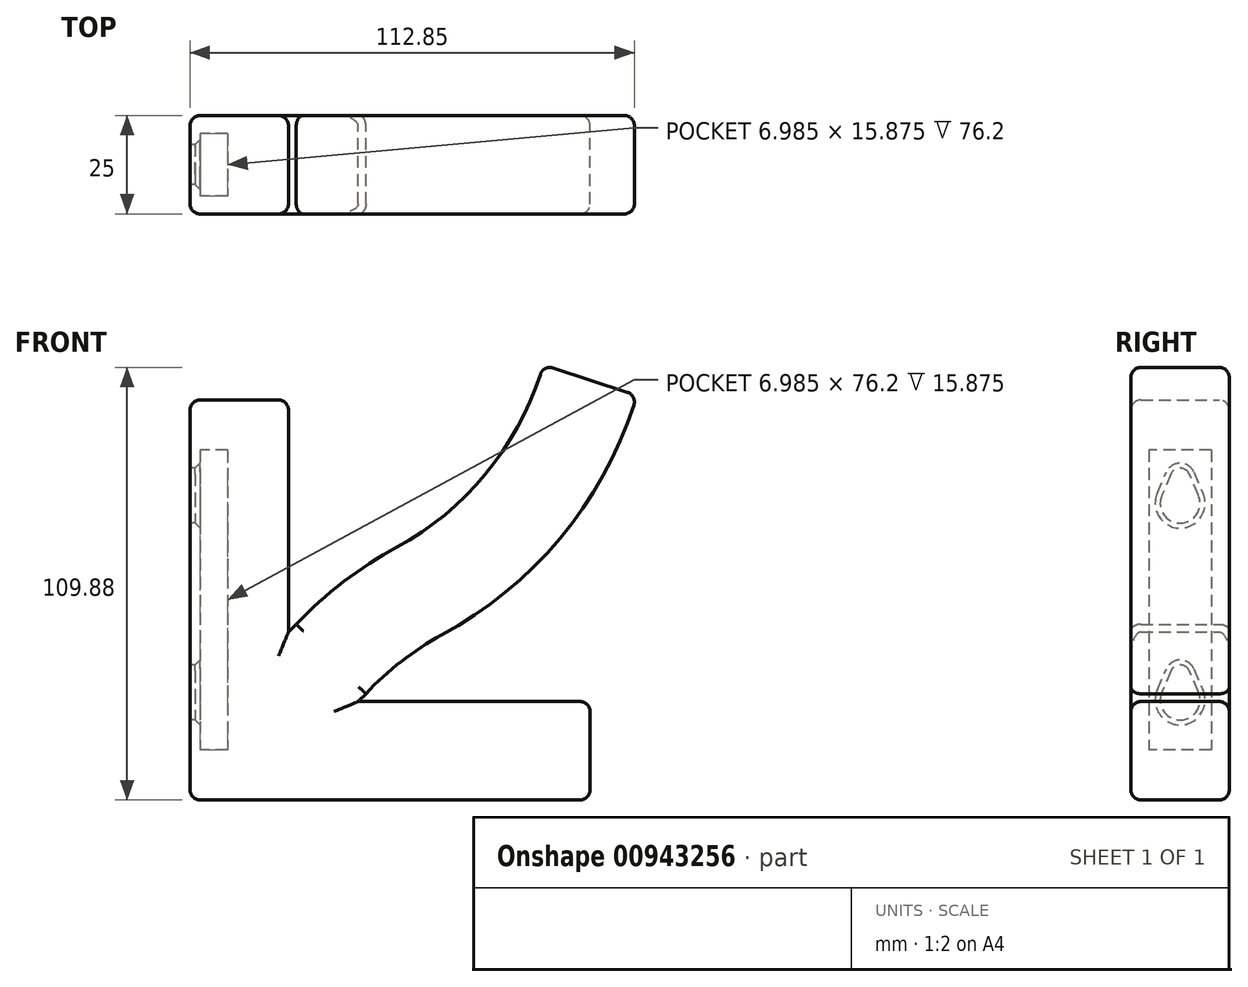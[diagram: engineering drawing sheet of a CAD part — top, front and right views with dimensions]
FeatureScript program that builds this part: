
annotation { "Feature Type Name" : "Feature", "Feature Type Description" : "" }
export const myFeature = defineFeature(function(context is Context, id is Id, definition is map)
    precondition{}
    {
        {
            var Q0;
            Q0=qCreatedBy(makeId("Front.planeOp"),FACE);
            var sketch = newSketch(context, id + "F0", { "sketchPlane" : qUnion([Q0])});
            skLineSegment(sketch, "E0", {"start": v(0, 0) * mm, "end": v(101.6, 0) * mm});
            skLineSegment(sketch, "E1", {"start": v(101.6, 0) * mm, "end": v(101.6, 25) * mm});
            skLineSegment(sketch, "E2", {"start": v(101.6, 25) * mm, "end": v(42.68, 25) * mm});
            skLineSegment(sketch, "E3", {"start": v(42.68, 25) * mm, "end": v(44.65, 26.98) * mm});
            skLineSegment(sketch, "E4", {"start": v(44.65, 26.98) * mm, "end": v(26.98, 44.65) * mm});
            skLineSegment(sketch, "E5", {"start": v(26.98, 44.65) * mm, "end": v(25, 42.68) * mm});
            skLineSegment(sketch, "E6", {"start": v(25, 42.68) * mm, "end": v(25, 101.6) * mm});
            skLineSegment(sketch, "E7", {"start": v(25, 101.6) * mm, "end": v(0, 101.6) * mm});
            skLineSegment(sketch, "E8", {"start": v(0, 101.6) * mm, "end": v(0, 0) * mm});
            skSolve(sketch);
        }
        {
            var Q0;
            Q0 = qSketchRegion(id + "F0", true);
            extrude(context, id + "F1", {"entities" : qUnion([Q0]), "depth" : 12.5 * mm, "offsetDistance" : 25.4 * mm, "hasSecondDirection" : true, "secondDirectionOppositeDirection" : true, "secondDirectionDepth" : 12.5 * mm});
        }
        {
            var Q0;
            Q0=qCreatedBy(makeId("Front.planeOp"),FACE);
            var sketch = newSketch(context, id + "F2", { "sketchPlane" : qUnion([Q0])});
            skArc(sketch, "E9", {"start": v(58.23, 53.06) * mm, "mid": v(46.33, 45.33) * mm, "end": v(35.81, 35.81) * mm});
            skArc(sketch, "E10", {"start": v(58.23, 53.06) * mm, "mid": v(85.26, 75.55) * mm, "end": v(101.6, 106.68) * mm});
            skSolve(sketch);
        }
        {
            var Q0;
            Q0=makeQuery(id+"F1.opExtrude","SWEPT_FACE",FACE,{"disambiguationData":[OSD([sQuery(id+"F0.wireOp",EDGE,"E4")])]});
            var sketch = newSketch(context, id + "F3", { "sketchPlane" : qUnion([Q0])});
            skLineSegment(sketch, "E11.0.0", {"start": v(12.5, -12.5) * mm, "end": v(12.5, 12.5) * mm});
            skLineSegment(sketch, "E11.0.1", {"start": v(12.5, 12.5) * mm, "end": v(-12.5, 12.5) * mm});
            skLineSegment(sketch, "E11.0.2", {"start": v(-12.5, 12.5) * mm, "end": v(-12.5, -12.5) * mm});
            skLineSegment(sketch, "E11.0.3", {"start": v(-12.5, -12.5) * mm, "end": v(12.5, -12.5) * mm});
            skSolve(sketch);
        }
        {
            var Q0;
            Q0 = qSketchRegion(id + "F3", true);
            var Q1;
            Q1 = qConstructionFilter(qBodyType(qCreatedBy(id + "F2" ,EDGE), BodyType.WIRE), ConstructionObject.NO);
            sweep(context, id + "F4", {"operationType" : NewBodyOperationType.ADD, "profiles" : qUnion([Q0]), "path" : qUnion([Q1])});
        }
        {
            var Q0;
            Q0=makeQuery(id+"F4.boolean.opBoolean","MERGE",FACE,{"derivedFrom":[makeQuery(id+"F1.opExtrude","CAP_FACE",FACE,{"disambiguationData":[OSD([sQuery(id+"F0.wireOp",EDGE,"E0"),sQuery(id+"F0.wireOp",EDGE,"E1"),sQuery(id+"F0.wireOp",EDGE,"E2"),sQuery(id+"F0.wireOp",EDGE,"E3"),sQuery(id+"F0.wireOp",EDGE,"E4"),sQuery(id+"F0.wireOp",EDGE,"E5"),sQuery(id+"F0.wireOp",EDGE,"E6"),sQuery(id+"F0.wireOp",EDGE,"E7"),sQuery(id+"F0.wireOp",EDGE,"E8")])],"isStart":false}),makeQuery(id+"F4.opSweep","SWEPT_FACE",FACE,{"disambiguationData":[OSD([sQuery(id+"F2.wireOp",EDGE,"E9"),sQuery(id+"F3.wireOp",EDGE,"E11.0.2")])]})]});
            var Q1;
            Q1=makeQuery(id+"F4.boolean.opBoolean","MERGE",FACE,{"derivedFrom":[makeQuery(id+"F1.opExtrude","CAP_FACE",FACE,{"disambiguationData":[OSD([sQuery(id+"F0.wireOp",EDGE,"E0"),sQuery(id+"F0.wireOp",EDGE,"E1"),sQuery(id+"F0.wireOp",EDGE,"E2"),sQuery(id+"F0.wireOp",EDGE,"E3"),sQuery(id+"F0.wireOp",EDGE,"E4"),sQuery(id+"F0.wireOp",EDGE,"E5"),sQuery(id+"F0.wireOp",EDGE,"E6"),sQuery(id+"F0.wireOp",EDGE,"E7"),sQuery(id+"F0.wireOp",EDGE,"E8")])],"isStart":true}),makeQuery(id+"F4.opSweep","SWEPT_FACE",FACE,{"disambiguationData":[OSD([sQuery(id+"F2.wireOp",EDGE,"E9"),sQuery(id+"F3.wireOp",EDGE,"E11.0.0")])]})]});
            var Q2;
            Q2=makeQuery(id+"F1.opExtrude","SWEPT_EDGE",EDGE,{"disambiguationData":[OSD([sQuery(id+"F0.wireOp",EDGE,"E0"),sQuery(id+"F0.wireOp",EDGE,"E1")])]});
            var Q3;
            Q3=makeQuery(id+"F1.opExtrude","SWEPT_EDGE",EDGE,{"disambiguationData":[OSD([sQuery(id+"F0.wireOp",EDGE,"E1"),sQuery(id+"F0.wireOp",EDGE,"E2")])]});
            var Q4;
            Q4=makeQuery(id+"F4.opSweep","CAP_EDGE",EDGE,{"disambiguationData":[OSD([sQuery(id+"F2.wireOp",VERTEX,"E10.end"),sQuery(id+"F3.wireOp",EDGE,"E11.0.3")])],"isStart":false});
            var Q5;
            Q5=makeQuery(id+"F4.opSweep","CAP_EDGE",EDGE,{"disambiguationData":[OSD([sQuery(id+"F2.wireOp",VERTEX,"E10.end"),sQuery(id+"F3.wireOp",EDGE,"E11.0.1")])],"isStart":false});
            var Q6;
            Q6=makeQuery(id+"F1.opExtrude","SWEPT_EDGE",EDGE,{"disambiguationData":[OSD([sQuery(id+"F0.wireOp",EDGE,"E6"),sQuery(id+"F0.wireOp",EDGE,"E7")])]});
            var Q7;
            Q7=makeQuery(id+"F1.opExtrude","SWEPT_EDGE",EDGE,{"disambiguationData":[OSD([sQuery(id+"F0.wireOp",EDGE,"E7"),sQuery(id+"F0.wireOp",EDGE,"E8")])]});
            var Q8;
            Q8=makeQuery(id+"F1.opExtrude","SWEPT_EDGE",EDGE,{"disambiguationData":[OSD([sQuery(id+"F0.wireOp",EDGE,"E0"),sQuery(id+"F0.wireOp",EDGE,"E8")])]});
            fillet(context, id + "F5", {"entities" : qUnion([Q0, Q1, Q2, Q3, Q4, Q5, Q6, Q7, Q8]), "radius" : 2.54 * mm, "tangentPropagation" : true, "allowEdgeOverflow" : false});
        }
        {
            var Q0;
            Q0=makeQuery(id+"F1.opExtrude","SWEPT_FACE",FACE,{"disambiguationData":[OSD([sQuery(id+"F0.wireOp",EDGE,"E8")])]});
            var sketch = newSketch(context, id + "F6", { "sketchPlane" : qUnion([Q0])});
            skLineSegment(sketch, "E12.bottom", {"start": v(-7.94, 88.9) * mm, "end": v(7.94, 88.9) * mm});
            skLineSegment(sketch, "E12.top", {"start": v(-7.94, 12.7) * mm, "end": v(7.94, 12.7) * mm});
            skLineSegment(sketch, "E12.left", {"start": v(-7.94, 88.9) * mm, "end": v(-7.94, 12.7) * mm});
            skLineSegment(sketch, "E12.right", {"start": v(7.94, 88.9) * mm, "end": v(7.94, 12.7) * mm});
            skLineSegment(sketch, "E13", {"start": v(0, 0) * mm, "end": v(0, 12.7) * mm, "construction": true});
            skSolve(sketch);
        }
        {
            var Q0;
            Q0 = qSketchRegion(id + "F6", true);
            extrude(context, id + "F7", {"entities" : qUnion([Q0]), "operationType" : NewBodyOperationType.REMOVE, "oppositeDirection" : true, "depth" : 9.52 * mm, "offsetDistance" : 25.4 * mm});
        }
        {
            var Q0;
            Q0=makeQuery(id+"F1.opExtrude","SWEPT_FACE",FACE,{"disambiguationData":[OSD([sQuery(id+"F0.wireOp",EDGE,"E8")])]});
            var sketch = newSketch(context, id + "F8", { "sketchPlane" : qUnion([Q0])});
            skLineSegment(sketch, "E14.bottom", {"start": v(-7.94, 88.9) * mm, "end": v(7.94, 88.9) * mm});
            skLineSegment(sketch, "E14.top", {"start": v(-7.94, 12.7) * mm, "end": v(7.94, 12.7) * mm});
            skLineSegment(sketch, "E14.left", {"start": v(-7.94, 88.9) * mm, "end": v(-7.94, 12.7) * mm});
            skLineSegment(sketch, "E14.right", {"start": v(7.94, 88.9) * mm, "end": v(7.94, 12.7) * mm});
            skCircle(sketch, "E15", {"center": v(0, 81.75) * mm, "radius": 2.54 * mm});
            skCircle(sketch, "E16", {"center": v(0, 31.75) * mm, "radius": 2.54 * mm});
            skCircle(sketch, "E17", {"center": v(0, 75.4) * mm, "radius": 5.08 * mm});
            skCircle(sketch, "E18", {"center": v(0, 25.4) * mm, "radius": 5.08 * mm});
            skLineSegment(sketch, "E19", {"start": v(-4.66, 27.43) * mm, "end": v(-2.33, 32.77) * mm});
            skLineSegment(sketch, "E20", {"start": v(2.33, 32.77) * mm, "end": v(4.66, 27.43) * mm});
            skLineSegment(sketch, "E21", {"start": v(-4.66, 77.43) * mm, "end": v(-2.33, 82.77) * mm});
            skLineSegment(sketch, "E22", {"start": v(2.33, 82.77) * mm, "end": v(4.66, 77.43) * mm});
            skSolve(sketch);
        }
        {
            var Q0;
            Q0 = qSketchRegion(id + "F8", true);
            extrude(context, id + "F9", {"entities" : qUnion([Q0]), "operationType" : NewBodyOperationType.ADD, "oppositeDirection" : true, "depth" : 2.54 * mm, "offsetDistance" : 25.4 * mm});
        }
        {
            var Q0;
            Q0=makeQuery(id+"F9.opExtrude","CAP_EDGE",EDGE,{"disambiguationData":[OSD([sQuery(id+"F8.wireOp",EDGE,"E15")])],"isStart":false});
            var Q1;
            Q1=makeQuery(id+"F9.opExtrude","CAP_EDGE",EDGE,{"disambiguationData":[OSD([sQuery(id+"F8.wireOp",EDGE,"E16")])],"isStart":false});
            chamfer(context, id + "F10", {"entities" : qUnion([Q0, Q1]), "width" : 1.27 * mm, "tangentPropagation" : true});
        }
    });
